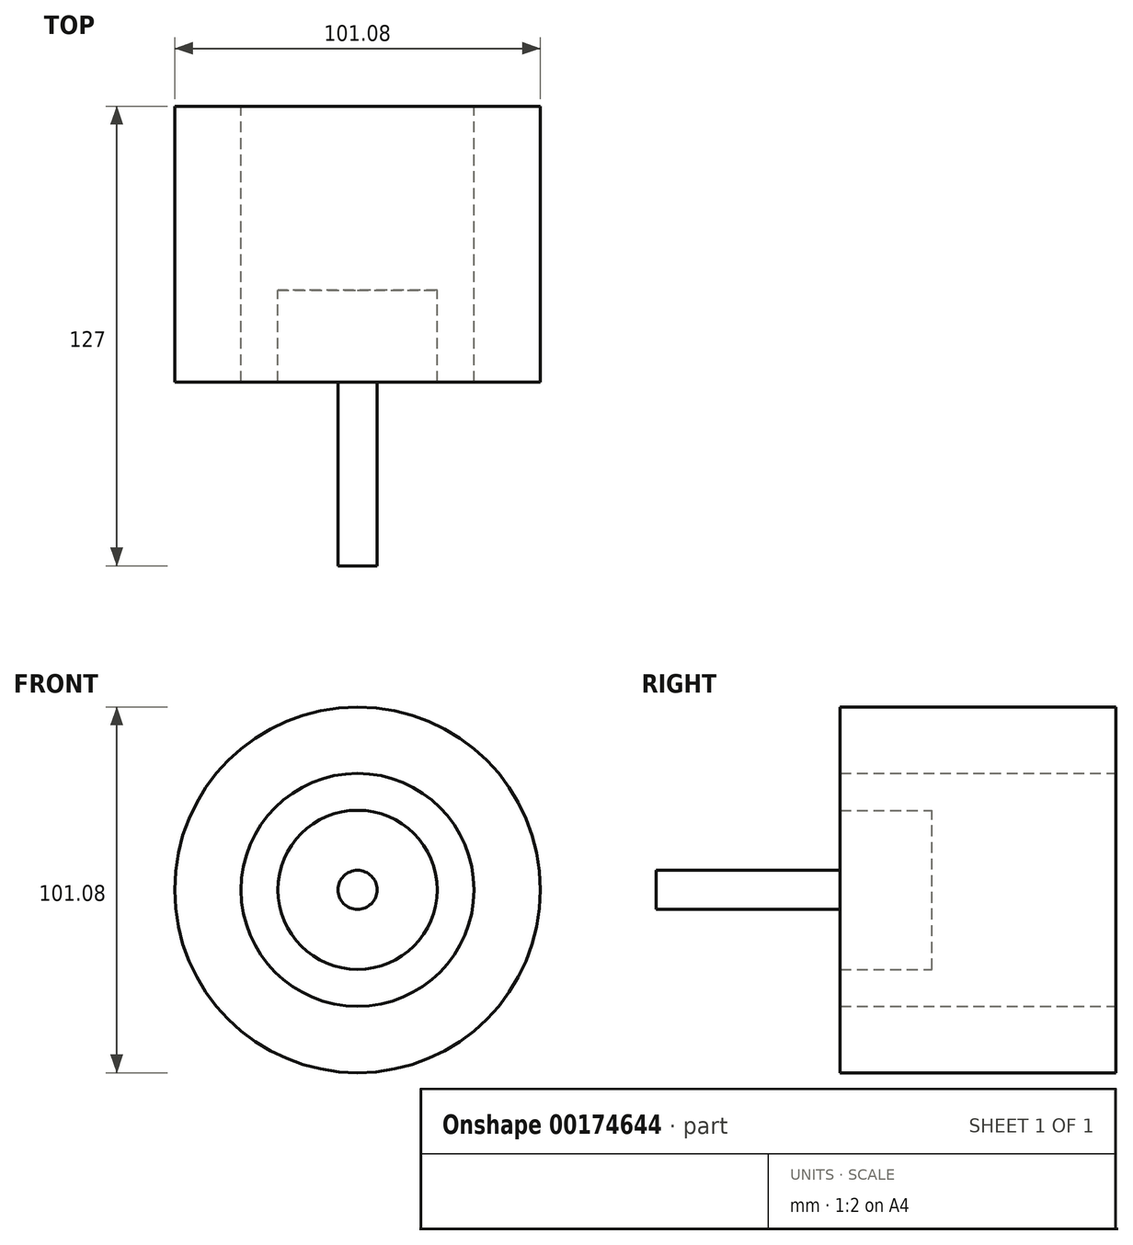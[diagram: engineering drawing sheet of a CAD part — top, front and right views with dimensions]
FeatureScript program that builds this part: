
annotation { "Feature Type Name" : "Feature", "Feature Type Description" : "" }
export const myFeature = defineFeature(function(context is Context, id is Id, definition is map)
    precondition{}
    {
        {
            var Q0;
            Q0=qCreatedBy(makeId("Front.planeOp"),FACE);
            var sketch = newSketch(context, id + "F0", { "sketchPlane" : qUnion([Q0])});
            skPoint(sketch, "E0.3.internal.orphan", {"position": v(-11.43, 32.75) * mm});
            skPoint(sketch, "E1.0.internal.orphan", {"position": v(68.89, 32.75) * mm});
            skPoint(sketch, "E1.2.internal.orphan", {"position": v(67.04, 32.75) * mm});
            skCircle(sketch, "E2", {"center": v(0, 0) * mm, "radius": 32.17 * mm});
            skCircle(sketch, "E3", {"center": v(0, 0) * mm, "radius": 5.4 * mm});
            skCircle(sketch, "E4", {"center": v(0, 0) * mm, "radius": 50.54 * mm});
            skSolve(sketch);
        }
        {
            var Q0;
            Q0=makeQuery(id+"F0.imprint","IMPRINT",FACE,{"disambiguationData":[TD([[makeQuery(id+"F0.imprint","IMPRINT",EDGE,{"derivedFrom":sQuery(id+"F0.wireOp",EDGE,"E2")}),-1.0]])]});
            var Q1;
            Q1=makeQuery(id+"F0.imprint","IMPRINT",FACE,{"disambiguationData":[TD([[makeQuery(id+"F0.imprint","IMPRINT",EDGE,{"derivedFrom":sQuery(id+"F0.wireOp",EDGE,"E3")}),1.0]])]});
            extrude(context, id + "F1", {"entities" : qUnion([Q0, Q1]), "depth" : 25.4 * mm});
        }
        {
            var Q0;
            Q0=makeQuery(id+"F1.opExtrude","CAP_FACE",FACE,{"disambiguationData":[OSD([sQuery(id+"F0.wireOp",EDGE,"E3")])],"isStart":false});
            extrude(context, id + "F2", {"entities" : qUnion([Q0]), "operationType" : NewBodyOperationType.ADD, "depth" : 50.8 * mm});
        }
        {
            var Q0;
            Q0=makeQuery(id+"F1.opExtrude","CAP_FACE",FACE,{"disambiguationData":[OSD([sQuery(id+"F0.wireOp",EDGE,"E2"),sQuery(id+"F0.wireOp",EDGE,"E4")])],"isStart":true});
            extrude(context, id + "F3", {"entities" : qUnion([Q0]), "operationType" : NewBodyOperationType.ADD, "depth" : 50.8 * mm});
        }
        {
            var Q0;
            Q0=qCreatedBy(makeId("Front.planeOp"),FACE);
            var sketch = newSketch(context, id + "F4", { "sketchPlane" : qUnion([Q0])});
            skCircle(sketch, "E5", {"center": v(0, 0) * mm, "radius": 21.99 * mm});
            skSolve(sketch);
        }
        {
            var Q0;
            Q0 = qSketchRegion(id + "F4", true);
            extrude(context, id + "F5", {"entities" : qUnion([Q0]), "operationType" : NewBodyOperationType.ADD, "depth" : 25.4 * mm});
        }
    });
